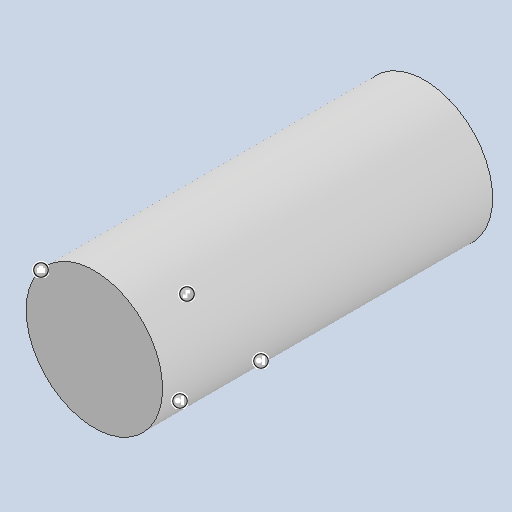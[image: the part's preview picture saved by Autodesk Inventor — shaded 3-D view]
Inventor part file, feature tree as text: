
AUTODESK INVENTOR PART (.ipt)
format: ipt  version: 2025.2 (Build 292293000, 293)  size: 205,312 bytes
history: native  units: mm
features: extrude x1
ambient origin geometry x8: Origin, YZ Plane, XZ Plane, XY Plane, X Axis, Y Axis, Z Axis, Center Point
bodies: Solid1 (feature_tree)
feature tree (1):
  extrude  "Extrusion1"  TaperAngle=0.0deg  [1 undecoded]
note: 1 required parameter value undecoded (feature->parameter linkage not recoverable at this tier; creation-order binding heuristic only, values carry confidence <= 0.55)
